# Revit family: Hager-UNIVERS-Surface_mounted-IP44-With_Cover-Without_DIN-NoHosted-NL-en
name_source: partatom
category: Electrical Equipment
units: mm (PartAtom-declared; Revit-internal decimal feet)

## family parameters
Always vertical = Yes
Cut with Voids When Loaded = No
Maintain Annotation Orientation = No
Panel Configuration = Two Columns, Circuits Across
Part Type = Panelboard
Room Calculation Point = No
Round Connector Dimension = Use Diameter
Shared = No
Work Plane-Based = Yes

## types (28) — shared parameters
Code hager = ADD-EC000214_EU
Default Elevation = 1200 mm
EF000003 - Mounting method = Surface mounted
EF000007 - Colour = White
EF000024 - UV resistant = No
EF000049 - Depth = 161 mm  [stored 0.528215 ft]
EF000116 - RAL-number = 9010
EF000118 - With mounting plate = No
EF001062 - EMC-version = No
EF001088 - Extension possible = Yes
EF001134 - DIN-rail = No
EF004462 - Type of closure = Other
EF005474 - Degree of protection (IP) = IP44
EF006244 - Transparent cover/door = No
EF006306 - With lock = No
EF009212 - Cover model = With notch
EF015776 - Earthing terminal block = No
EF015777 - Neutral terminal block = No
EF015941 - Signal passing door = No
ETIM class code = EC000214
ETIM class name = Small distribution board
HG000002-With door or cover = Yes
HG000003-Range = UNIVERS
HG000005-Thickness = 2 mm  [stored 0.00656168 ft]
HG000006-Flush mounted = No
HG000011-Empty rows from bottom = No
HG000012-Door swing angle = 90.00°
HG000013-Door on the left = No
HG000014-Door on the right = Yes
HG000015-Clearance visibility = Yes
HG000016-Door 3D visibility = Yes
HG000017-Distance between poles = 18 mm  [stored 0.0590551 ft]
HG000060-RAL-number = 9010
HG000099-Onfly Template ID = 507532
Manufacturer = Hager
Name BIM&CO = Electricity
Name hager = ADD_Enclosures_EC000214
Reference = Template-Enclosure_EU-EC000214
Uniformat = Low Tension Service & Dist.
Uniformat code = D501001
zero-valued in all types: EF001131 - Inner depth, HG000007-Number of empty columns

## per-type parameters (varying)
| type | BC_METADATA | EF000008 - Width | EF000040 - Height | EF000218 - Built-in depth | EF000266 - Number of rows | EF000332 - Built-in height | EF000846 - Built-in width | EF002950 - Width in number of modular spacings | HG000001-Number of columns | HG000004-Manufacturer reference | HG000008-Number of empty rows | HG000009-Double swing door | HG000010-Asymmetric doors | HGEF000266-Number of rows | HGEF002950-Width in number of modular spacings |
| UNIVERS-Surface_mounted_W550_H800_D161_24_Modular_Spacing-FWQ52N | {"ObjectGuid":"ee0aeab5-1081-47b9-ade3-4cf7be4a64a3","ModelGuid":"6c336c6b-cede-4711-8bec-980dfd7acaf8","VariantGuid":"ffe9debf-ef32-43b4-9df7-37f38c4a8643","Revision":"#3","VariantName":"UNIVERS-Surface_mounted_W550_H800_D161_24_Modular_Spacing-FWQ52N"} | 550 mm  [stored 1.80446 ft] | 800 mm  [stored 2.62467 ft] | 0 mm  [stored 0 ft] | 5 | 800 mm  [stored 2.62467 ft] | 550 mm  [stored 1.80446 ft] | 24 | 2 | FWQ52N | 2 | No | No | 5 | 24 |
| UNIVERS-Surface_mounted_W550_H800_D161_24_Modular_Spacing-FWQ52P | {"ObjectGuid":"ee0aeab5-1081-47b9-ade3-4cf7be4a64a3","ModelGuid":"6c336c6b-cede-4711-8bec-980dfd7acaf8","VariantGuid":"240f952e-ef19-4097-bef8-52be47afbbdb","Revision":"#3","VariantName":"UNIVERS-Surface_mounted_W550_H800_D161_24_Modular_Spacing-FWQ52P"} | 550 mm  [stored 1.80446 ft] | 800 mm  [stored 2.62467 ft] | 161 mm  [stored 0.528215 ft] | 5 | 800 mm  [stored 2.62467 ft] | 550 mm  [stored 1.80446 ft] | 24 | 2 | FWQ52P | 0 | No | No | 5 | 24 |
| UNIVERS-Surface_mounted_W800_H800_D161_36_Modular_Spacing-FWQ53N | {"ObjectGuid":"ee0aeab5-1081-47b9-ade3-4cf7be4a64a3","ModelGuid":"6c336c6b-cede-4711-8bec-980dfd7acaf8","VariantGuid":"2a32d502-9165-49f1-b18e-9b88de7edb8c","Revision":"#3","VariantName":"UNIVERS-Surface_mounted_W800_H800_D161_36_Modular_Spacing-FWQ53N"} | 800 mm  [stored 2.62467 ft] | 800 mm  [stored 2.62467 ft] | 161 mm  [stored 0.528215 ft] | 5 | 800 mm  [stored 2.62467 ft] | 800 mm  [stored 2.62467 ft] | 36 | 3 | FWQ53N | 2 | Yes | Yes | 5 | 36 |
| UNIVERS-Surface_mounted_W800_H800_D161_36_Modular_Spacing-FWQ53P | {"ObjectGuid":"ee0aeab5-1081-47b9-ade3-4cf7be4a64a3","ModelGuid":"6c336c6b-cede-4711-8bec-980dfd7acaf8","VariantGuid":"60c0ce25-8d45-41bc-aca0-486f2597c990","Revision":"#3","VariantName":"UNIVERS-Surface_mounted_W800_H800_D161_36_Modular_Spacing-FWQ53P"} | 800 mm  [stored 2.62467 ft] | 800 mm  [stored 2.62467 ft] | 0 mm  [stored 0 ft] | 5 | 800 mm  [stored 2.62467 ft] | 800 mm  [stored 2.62467 ft] | 36 | 3 | FWQ53P | 0 | Yes | Yes | 5 | 36 |
| UNIVERS-Surface_mounted_W1050_H800_D161_48_Modular_Spacing-FWQ54P | {"ObjectGuid":"ee0aeab5-1081-47b9-ade3-4cf7be4a64a3","ModelGuid":"6c336c6b-cede-4711-8bec-980dfd7acaf8","VariantGuid":"2c29d696-9a53-4e92-96ac-c91360afbcbb","Revision":"#3","VariantName":"UNIVERS-Surface_mounted_W1050_H800_D161_48_Modular_Spacing-FWQ54P"} | 1050 mm | 800 mm  [stored 2.62467 ft] | 0 mm  [stored 0 ft] | 5 | 800 mm  [stored 2.62467 ft] | 1050 mm | 48 | 4 | FWQ54P | 0 | Yes | No | 5 | 48 |
| UNIVERS-Surface_mounted_W300_H950_D161_12_Modular_Spacing-FWQ61P | {"ObjectGuid":"ee0aeab5-1081-47b9-ade3-4cf7be4a64a3","ModelGuid":"6c336c6b-cede-4711-8bec-980dfd7acaf8","VariantGuid":"ff9733c0-62c9-42ae-8dd0-f3fa578bd38f","Revision":"#3","VariantName":"UNIVERS-Surface_mounted_W300_H950_D161_12_Modular_Spacing-FWQ61P"} | 300 mm | 950 mm  [stored 3.1168 ft] | 0 mm  [stored 0 ft] | 6 | 950 mm  [stored 3.1168 ft] | 300 mm | 12 | 1 | FWQ61P | 0 | No | No | 6 | 12 |
| UNIVERS-Surface_mounted_W300_H500_D161_12_Modular_Spacing-FWQ31P | {"ObjectGuid":"ee0aeab5-1081-47b9-ade3-4cf7be4a64a3","ModelGuid":"6c336c6b-cede-4711-8bec-980dfd7acaf8","VariantGuid":"57722745-67e7-4336-8d34-298b5b02bc30","Revision":"#3","VariantName":"UNIVERS-Surface_mounted_W300_H500_D161_12_Modular_Spacing-FWQ31P"} | 300 mm | 500 mm  [stored 1.64042 ft] | 0 mm  [stored 0 ft] | 3 | 500 mm  [stored 1.64042 ft] | 300 mm | 12 | 1 | FWQ31P | 0 | No | No | 3 | 12 |
| UNIVERS-Surface_mounted_W550_H500_D161_24_Modular_Spacing-FWQ32P | {"ObjectGuid":"ee0aeab5-1081-47b9-ade3-4cf7be4a64a3","ModelGuid":"6c336c6b-cede-4711-8bec-980dfd7acaf8","VariantGuid":"ac9333a7-b402-4183-a3c6-3c21e74443ae","Revision":"#3","VariantName":"UNIVERS-Surface_mounted_W550_H500_D161_24_Modular_Spacing-FWQ32P"} | 550 mm  [stored 1.80446 ft] | 500 mm  [stored 1.64042 ft] | 161 mm  [stored 0.528215 ft] | 3 | 500 mm  [stored 1.64042 ft] | 550 mm  [stored 1.80446 ft] | 24 | 2 | FWQ32P | 0 | No | No | 3 | 24 |
| UNIVERS-Surface_mounted_W800_H500_D161_36_Modular_Spacing-FWQ33P | {"ObjectGuid":"ee0aeab5-1081-47b9-ade3-4cf7be4a64a3","ModelGuid":"6c336c6b-cede-4711-8bec-980dfd7acaf8","VariantGuid":"a9653296-f252-45a0-9f87-8876396c97b6","Revision":"#3","VariantName":"UNIVERS-Surface_mounted_W800_H500_D161_36_Modular_Spacing-FWQ33P"} | 800 mm  [stored 2.62467 ft] | 500 mm  [stored 1.64042 ft] | 0 mm  [stored 0 ft] | 3 | 500 mm  [stored 1.64042 ft] | 800 mm  [stored 2.62467 ft] | 36 | 3 | FWQ33P | 0 | Yes | Yes | 3 | 36 |
| UNIVERS-Surface_mounted_W1050_H500_D161_48_Modular_Spacing-FWQ34P | {"ObjectGuid":"ee0aeab5-1081-47b9-ade3-4cf7be4a64a3","ModelGuid":"6c336c6b-cede-4711-8bec-980dfd7acaf8","VariantGuid":"2098ac63-f459-431b-9c37-18ec10078308","Revision":"#3","VariantName":"UNIVERS-Surface_mounted_W1050_H500_D161_48_Modular_Spacing-FWQ34P"} | 1050 mm | 500 mm  [stored 1.64042 ft] | 0 mm  [stored 0 ft] | 3 | 500 mm  [stored 1.64042 ft] | 1050 mm | 48 | 4 | FWQ34P | 0 | Yes | No | 3 | 48 |
| UNIVERS-Surface_mounted_W300_H650_D161_12_Modular_Spacing-FWQ41P | {"ObjectGuid":"ee0aeab5-1081-47b9-ade3-4cf7be4a64a3","ModelGuid":"6c336c6b-cede-4711-8bec-980dfd7acaf8","VariantGuid":"c1761af8-c559-4f46-b9bd-eb0186f99840","Revision":"#3","VariantName":"UNIVERS-Surface_mounted_W300_H650_D161_12_Modular_Spacing-FWQ41P"} | 300 mm | 650 mm  [stored 2.13255 ft] | 0 mm  [stored 0 ft] | 4 | 650 mm  [stored 2.13255 ft] | 300 mm | 12 | 1 | FWQ41P | 0 | No | No | 4 | 12 |
| UNIVERS-Surface_mounted_W550_H650_D161_24_Modular_Spacing-FWQ42P | {"ObjectGuid":"ee0aeab5-1081-47b9-ade3-4cf7be4a64a3","ModelGuid":"6c336c6b-cede-4711-8bec-980dfd7acaf8","VariantGuid":"f5485f72-e956-466e-aada-41c5b0b97b1d","Revision":"#3","VariantName":"UNIVERS-Surface_mounted_W550_H650_D161_24_Modular_Spacing-FWQ42P"} | 550 mm  [stored 1.80446 ft] | 650 mm  [stored 2.13255 ft] | 0 mm  [stored 0 ft] | 4 | 650 mm  [stored 2.13255 ft] | 550 mm  [stored 1.80446 ft] | 24 | 2 | FWQ42P | 0 | No | No | 4 | 24 |
| UNIVERS-Surface_mounted_W800_H650_D161_36_Modular_Spacing-FWQ43P | {"ObjectGuid":"ee0aeab5-1081-47b9-ade3-4cf7be4a64a3","ModelGuid":"6c336c6b-cede-4711-8bec-980dfd7acaf8","VariantGuid":"dcc165c5-d235-4a07-9fc7-83f5c62cdd5e","Revision":"#3","VariantName":"UNIVERS-Surface_mounted_W800_H650_D161_36_Modular_Spacing-FWQ43P"} | 800 mm  [stored 2.62467 ft] | 650 mm  [stored 2.13255 ft] | 0 mm  [stored 0 ft] | 4 | 650 mm  [stored 2.13255 ft] | 800 mm  [stored 2.62467 ft] | 36 | 3 | FWQ43P | 0 | Yes | Yes | 4 | 36 |
| UNIVERS-Surface_mounted_W1050_H650_D161_48_Modular_Spacing-FWQ44P | {"ObjectGuid":"ee0aeab5-1081-47b9-ade3-4cf7be4a64a3","ModelGuid":"6c336c6b-cede-4711-8bec-980dfd7acaf8","VariantGuid":"01542c18-ede2-47f4-98fc-4317cb434a61","Revision":"#3","VariantName":"UNIVERS-Surface_mounted_W1050_H650_D161_48_Modular_Spacing-FWQ44P"} | 1050 mm | 650 mm  [stored 2.13255 ft] | 0 mm  [stored 0 ft] | 4 | 650 mm  [stored 2.13255 ft] | 1050 mm | 48 | 4 | FWQ44P | 0 | Yes | No | 4 | 48 |
| UNIVERS-Surface_mounted_W300_H800_D161_12_Modular_Spacing-FWQ51P | {"ObjectGuid":"ee0aeab5-1081-47b9-ade3-4cf7be4a64a3","ModelGuid":"6c336c6b-cede-4711-8bec-980dfd7acaf8","VariantGuid":"d679bf2d-391e-48ff-9f55-acb524b89824","Revision":"#3","VariantName":"UNIVERS-Surface_mounted_W300_H800_D161_12_Modular_Spacing-FWQ51P"} | 300 mm | 800 mm  [stored 2.62467 ft] | 0 mm  [stored 0 ft] | 5 | 800 mm  [stored 2.62467 ft] | 300 mm | 12 | 1 | FWQ51P | 0 | No | No | 5 | 12 |
| UNIVERS-Surface_mounted_W550_H950_D161_24_Modular_Spacing-FWQ62N | {"ObjectGuid":"ee0aeab5-1081-47b9-ade3-4cf7be4a64a3","ModelGuid":"6c336c6b-cede-4711-8bec-980dfd7acaf8","VariantGuid":"ddcb862c-f6d7-45f0-b5d4-a90b085c9f7b","Revision":"#3","VariantName":"UNIVERS-Surface_mounted_W550_H950_D161_24_Modular_Spacing-FWQ62N"} | 550 mm  [stored 1.80446 ft] | 950 mm  [stored 3.1168 ft] | 0 mm  [stored 0 ft] | 6 | 950 mm  [stored 3.1168 ft] | 550 mm  [stored 1.80446 ft] | 24 | 2 | FWQ62N | 2 | No | No | 6 | 24 |
| UNIVERS-Surface_mounted_W550_H950_D161_24_Modular_Spacing-FWQ62P | {"ObjectGuid":"ee0aeab5-1081-47b9-ade3-4cf7be4a64a3","ModelGuid":"6c336c6b-cede-4711-8bec-980dfd7acaf8","VariantGuid":"366119de-d223-4637-a8b3-a163391010c9","Revision":"#3","VariantName":"UNIVERS-Surface_mounted_W550_H950_D161_24_Modular_Spacing-FWQ62P"} | 550 mm  [stored 1.80446 ft] | 950 mm  [stored 3.1168 ft] | 161 mm  [stored 0.528215 ft] | 6 | 950 mm  [stored 3.1168 ft] | 550 mm  [stored 1.80446 ft] | 24 | 2 | FWQ62P | 0 | No | No | 6 | 24 |
| UNIVERS-Surface_mounted_W800_H950_D161_36_Modular_Spacing-FWQ63N | {"ObjectGuid":"ee0aeab5-1081-47b9-ade3-4cf7be4a64a3","ModelGuid":"6c336c6b-cede-4711-8bec-980dfd7acaf8","VariantGuid":"ccd84e1c-f424-449a-a319-3da54072c6f3","Revision":"#3","VariantName":"UNIVERS-Surface_mounted_W800_H950_D161_36_Modular_Spacing-FWQ63N"} | 800 mm  [stored 2.62467 ft] | 950 mm  [stored 3.1168 ft] | 161 mm  [stored 0.528215 ft] | 6 | 950 mm  [stored 3.1168 ft] | 800 mm  [stored 2.62467 ft] | 36 | 3 | FWQ63N | 2 | Yes | Yes | 6 | 36 |
| UNIVERS-Surface_mounted_W800_H950_D161_36_Modular_Spacing-FWQ63P | {"ObjectGuid":"ee0aeab5-1081-47b9-ade3-4cf7be4a64a3","ModelGuid":"6c336c6b-cede-4711-8bec-980dfd7acaf8","VariantGuid":"e17b5849-4acb-4831-9bd7-fda7226bf1bf","Revision":"#3","VariantName":"UNIVERS-Surface_mounted_W800_H950_D161_36_Modular_Spacing-FWQ63P"} | 800 mm  [stored 2.62467 ft] | 950 mm  [stored 3.1168 ft] | 0 mm  [stored 0 ft] | 6 | 950 mm  [stored 3.1168 ft] | 800 mm  [stored 2.62467 ft] | 36 | 3 | FWQ63P | 0 | Yes | Yes | 6 | 36 |
| UNIVERS-Surface_mounted_W1050_H950_D161_48_Modular_Spacing-FWQ64N | {"ObjectGuid":"ee0aeab5-1081-47b9-ade3-4cf7be4a64a3","ModelGuid":"6c336c6b-cede-4711-8bec-980dfd7acaf8","VariantGuid":"8829867c-c65d-4cf3-8df0-9ef2f92ba0e0","Revision":"#3","VariantName":"UNIVERS-Surface_mounted_W1050_H950_D161_48_Modular_Spacing-FWQ64N"} | 1050 mm | 950 mm  [stored 3.1168 ft] | 0 mm  [stored 0 ft] | 6 | 950 mm  [stored 3.1168 ft] | 1050 mm | 48 | 4 | FWQ64N | 2 | Yes | No | 6 | 48 |
| UNIVERS-Surface_mounted_W1050_H950_D161_48_Modular_Spacing-FWQ64P | {"ObjectGuid":"ee0aeab5-1081-47b9-ade3-4cf7be4a64a3","ModelGuid":"6c336c6b-cede-4711-8bec-980dfd7acaf8","VariantGuid":"d5cd7e30-5b5a-4c07-a0ec-1fe3ea5432a8","Revision":"#3","VariantName":"UNIVERS-Surface_mounted_W1050_H950_D161_48_Modular_Spacing-FWQ64P"} | 1050 mm | 950 mm  [stored 3.1168 ft] | 161 mm  [stored 0.528215 ft] | 6 | 950 mm  [stored 3.1168 ft] | 1050 mm | 48 | 4 | FWQ64P | 0 | Yes | No | 6 | 48 |
| UNIVERS-Surface_mounted_W300_H1100_D161_12_Modular_Spacing-FWQ71P | {"ObjectGuid":"ee0aeab5-1081-47b9-ade3-4cf7be4a64a3","ModelGuid":"6c336c6b-cede-4711-8bec-980dfd7acaf8","VariantGuid":"3c909781-ab07-4558-86df-165d3c4e84e1","Revision":"#3","VariantName":"UNIVERS-Surface_mounted_W300_H1100_D161_12_Modular_Spacing-FWQ71P"} | 300 mm | 1100 mm | 161 mm  [stored 0.528215 ft] | 7 | 1100 mm | 300 mm | 12 | 1 | FWQ71P | 0 | No | No | 7 | 12 |
| UNIVERS-Surface_mounted_W550_H1100_D161_24_Modular_Spacing-FWQ72N | {"ObjectGuid":"ee0aeab5-1081-47b9-ade3-4cf7be4a64a3","ModelGuid":"6c336c6b-cede-4711-8bec-980dfd7acaf8","VariantGuid":"57117a71-6de5-43aa-a5b0-78d5eb7211a6","Revision":"#3","VariantName":"UNIVERS-Surface_mounted_W550_H1100_D161_24_Modular_Spacing-FWQ72N"} | 550 mm  [stored 1.80446 ft] | 1100 mm | 161 mm  [stored 0.528215 ft] | 7 | 1100 mm | 550 mm  [stored 1.80446 ft] | 24 | 2 | FWQ72N | 2 | No | No | 7 | 24 |
| UNIVERS-Surface_mounted_W550_H1100_D161_12_Modular_Spacing-FWQ72P | {"ObjectGuid":"ee0aeab5-1081-47b9-ade3-4cf7be4a64a3","ModelGuid":"6c336c6b-cede-4711-8bec-980dfd7acaf8","VariantGuid":"52c0bdf8-e31b-4c34-a46d-bed44e0e2f4e","Revision":"#3","VariantName":"UNIVERS-Surface_mounted_W550_H1100_D161_12_Modular_Spacing-FWQ72P"} | 550 mm  [stored 1.80446 ft] | 1100 mm | 0 mm  [stored 0 ft] | 7 | 1100 mm | 550 mm  [stored 1.80446 ft] | 12 | 2 | FWQ72P | 0 | No | No | 7 | 12 |
| UNIVERS-Surface_mounted_W800_H1100_D161_36_Modular_Spacing-FWQ73N | {"ObjectGuid":"ee0aeab5-1081-47b9-ade3-4cf7be4a64a3","ModelGuid":"6c336c6b-cede-4711-8bec-980dfd7acaf8","VariantGuid":"197aa896-126a-4002-872c-760864ae0f63","Revision":"#3","VariantName":"UNIVERS-Surface_mounted_W800_H1100_D161_36_Modular_Spacing-FWQ73N"} | 800 mm  [stored 2.62467 ft] | 1100 mm | 0 mm  [stored 0 ft] | 7 | 1100 mm | 800 mm  [stored 2.62467 ft] | 36 | 3 | FWQ73N | 2 | Yes | Yes | 7 | 36 |
| UNIVERS-Surface_mounted_W800_H1100_D161_12_Modular_Spacing-FWQ73P | {"ObjectGuid":"ee0aeab5-1081-47b9-ade3-4cf7be4a64a3","ModelGuid":"6c336c6b-cede-4711-8bec-980dfd7acaf8","VariantGuid":"99578657-722c-4624-a13c-5f3a52f64d4a","Revision":"#3","VariantName":"UNIVERS-Surface_mounted_W800_H1100_D161_12_Modular_Spacing-FWQ73P"} | 800 mm  [stored 2.62467 ft] | 1100 mm | 161 mm  [stored 0.528215 ft] | 7 | 1100 mm | 800 mm  [stored 2.62467 ft] | 12 | 3 | FWQ73P | 0 | Yes | Yes | 7 | 12 |
| UNIVERS-Surface_mounted_W1050_H1100_D161_48_Modular_Spacing-FWQ74N | {"ObjectGuid":"ee0aeab5-1081-47b9-ade3-4cf7be4a64a3","ModelGuid":"6c336c6b-cede-4711-8bec-980dfd7acaf8","VariantGuid":"c368aa43-3d51-4900-8c92-36cfd7fcc560","Revision":"#3","VariantName":"UNIVERS-Surface_mounted_W1050_H1100_D161_48_Modular_Spacing-FWQ74N"} | 1050 mm | 1100 mm | 161 mm  [stored 0.528215 ft] | 7 | 1100 mm | 1050 mm | 48 | 4 | FWQ74N | 2 | Yes | No | 7 | 48 |
| UNIVERS-Surface_mounted_W1050_H1100_D161_12_Modular_Spacing-FWQ74P | {"ObjectGuid":"ee0aeab5-1081-47b9-ade3-4cf7be4a64a3","ModelGuid":"6c336c6b-cede-4711-8bec-980dfd7acaf8","VariantGuid":"6cb12132-12f5-41bf-a453-9cb102a6e872","Revision":"#3","VariantName":"UNIVERS-Surface_mounted_W1050_H1100_D161_12_Modular_Spacing-FWQ74P"} | 1050 mm | 1100 mm | 161 mm  [stored 0.528215 ft] | 7 | 1100 mm | 1050 mm | 12 | 4 | FWQ74P | 0 | Yes | No | 7 | 12 |

note: [stored X ft] marks values corroborated as IEEE doubles in the binary element streams (Revit-internal decimal feet)

## geometry (parser evidence)
native form markers: Sweep x14
no freeform markers — native parametric forms only
